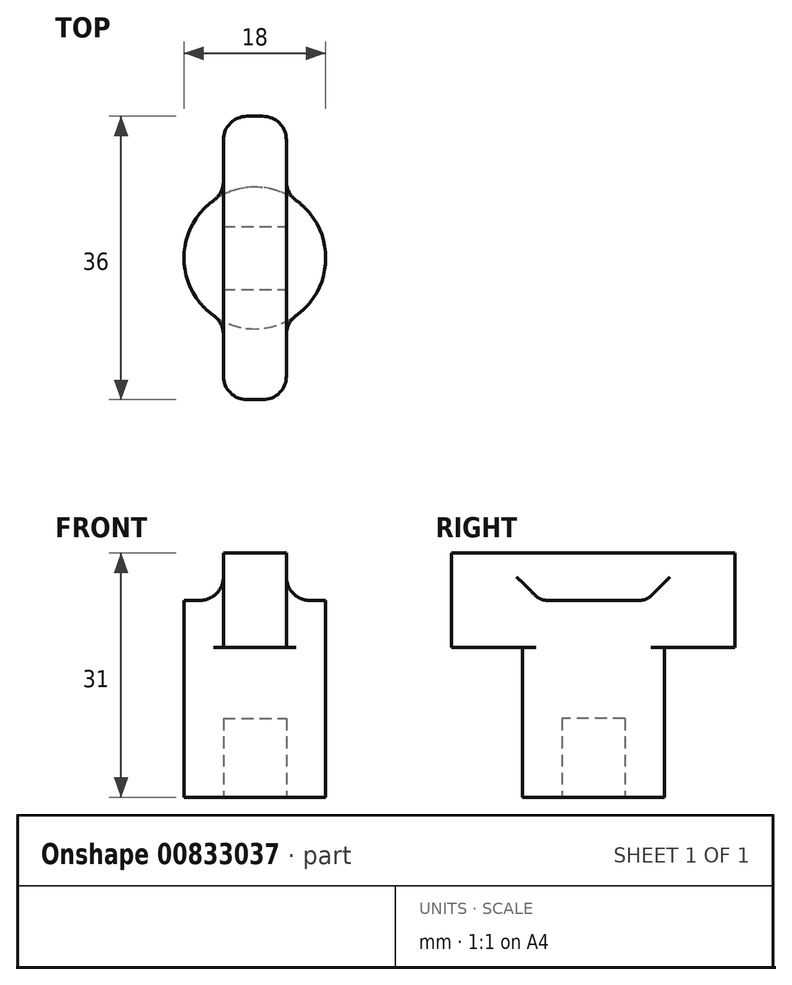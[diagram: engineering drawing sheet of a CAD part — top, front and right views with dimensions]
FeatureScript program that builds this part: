
annotation { "Feature Type Name" : "Feature", "Feature Type Description" : "" }
export const myFeature = defineFeature(function(context is Context, id is Id, definition is map)
    precondition{}
    {
        {
            var Q0;
            Q0=qCreatedBy(makeId("Top.planeOp"),FACE);
            var sketch = newSketch(context, id + "F0", { "sketchPlane" : qUnion([Q0])});
            skCircle(sketch, "E0", {"center": v(0, 0) * mm, "radius": 9 * mm});
            skSolve(sketch);
        }
        {
            var Q0;
            Q0 = qSketchRegion(id + "F0", true);
            extrude(context, id + "F1", {"entities" : qUnion([Q0]), "depth" : 25 * mm, "offsetDistance" : 25 * mm});
        }
        {
            var Q0;
            Q0=makeQuery(id+"F1.opExtrude","CAP_FACE",FACE,{"disambiguationData":[OSD([sQuery(id+"F0.wireOp",EDGE,"E0")])],"isStart":true});
            var sketch = newSketch(context, id + "F2", { "sketchPlane" : qUnion([Q0])});
            skLineSegment(sketch, "E1.bottom", {"start": v(-4, -4) * mm, "end": v(4, -4) * mm});
            skLineSegment(sketch, "E1.top", {"start": v(-4, 4) * mm, "end": v(4, 4) * mm});
            skLineSegment(sketch, "E1.left", {"start": v(-4, -4) * mm, "end": v(-4, 4) * mm});
            skLineSegment(sketch, "E1.right", {"start": v(4, -4) * mm, "end": v(4, 4) * mm});
            skSolve(sketch);
        }
        {
            var Q0;
            Q0 = qSketchRegion(id + "F2", true);
            extrude(context, id + "F3", {"entities" : qUnion([Q0]), "operationType" : NewBodyOperationType.REMOVE, "oppositeDirection" : true, "depth" : 10 * mm, "offsetDistance" : 25 * mm});
        }
        {
            var Q0;
            Q0=makeQuery(id+"F1.opExtrude","CAP_FACE",FACE,{"disambiguationData":[OSD([sQuery(id+"F0.wireOp",EDGE,"E0")])],"isStart":false});
            var sketch = newSketch(context, id + "F4", { "sketchPlane" : qUnion([Q0])});
            skLineSegment(sketch, "E2.bottom", {"start": v(-4, -18) * mm, "end": v(4, -18) * mm});
            skLineSegment(sketch, "E2.top", {"start": v(-4, 18) * mm, "end": v(4, 18) * mm});
            skLineSegment(sketch, "E2.left", {"start": v(-4, -18) * mm, "end": v(-4, 18) * mm});
            skLineSegment(sketch, "E2.right", {"start": v(4, -18) * mm, "end": v(4, 18) * mm});
            skSolve(sketch);
        }
        {
            var Q0;
            Q0 = qSketchRegion(id + "F4", true);
            extrude(context, id + "F5", {"entities" : qUnion([Q0]), "operationType" : NewBodyOperationType.ADD, "endBound" : BoundingType.SYMMETRIC, "depth" : 12 * mm, "offsetDistance" : 25 * mm});
        }
        {
            var Q0;
            Q0=makeQuery(id+"F5.opExtrude","SWEPT_EDGE",EDGE,{"disambiguationData":[OSD([sQuery(id+"F4.wireOp",EDGE,"E2.top"),sQuery(id+"F4.wireOp",EDGE,"E2.left")])]});
            var Q1;
            Q1=makeQuery(id+"F5.opExtrude","SWEPT_EDGE",EDGE,{"disambiguationData":[OSD([sQuery(id+"F4.wireOp",EDGE,"E2.top"),sQuery(id+"F4.wireOp",EDGE,"E2.right")])]});
            var Q2;
            Q2=makeQuery(id+"F5.opExtrude","SWEPT_EDGE",EDGE,{"disambiguationData":[OSD([sQuery(id+"F4.wireOp",EDGE,"E2.bottom"),sQuery(id+"F4.wireOp",EDGE,"E2.left")])]});
            var Q3;
            Q3=makeQuery(id+"F5.opExtrude","SWEPT_EDGE",EDGE,{"disambiguationData":[OSD([sQuery(id+"F4.wireOp",EDGE,"E2.bottom"),sQuery(id+"F4.wireOp",EDGE,"E2.right")])]});
            var Q4;
            Q4=makeQuery(id+"F5.boolean.opBoolean","INTERSECT",EDGE,{"derivedFrom":[makeQuery(id+"F1.opExtrude","CAP_FACE",FACE,{"disambiguationData":[OSD([sQuery(id+"F0.wireOp",EDGE,"E0")])],"isStart":false}),makeQuery(id+"F5.opExtrude","SWEPT_FACE",FACE,{"disambiguationData":[OSD([sQuery(id+"F4.wireOp",EDGE,"E2.left")])]})]});
            var Q5;
            Q5=makeQuery(id+"F5.boolean.opBoolean","INTERSECT",EDGE,{"disambiguationData":[OD(1.0)],"derivedFrom":[makeQuery(id+"F1.opExtrude","SWEPT_FACE",FACE,{"disambiguationData":[OSD([sQuery(id+"F0.wireOp",EDGE,"E0")])]}),makeQuery(id+"F5.opExtrude","SWEPT_FACE",FACE,{"disambiguationData":[OSD([sQuery(id+"F4.wireOp",EDGE,"E2.left")])]})]});
            var Q6;
            Q6=makeQuery(id+"F5.boolean.opBoolean","INTERSECT",EDGE,{"disambiguationData":[OD(0.0)],"derivedFrom":[makeQuery(id+"F1.opExtrude","SWEPT_FACE",FACE,{"disambiguationData":[OSD([sQuery(id+"F0.wireOp",EDGE,"E0")])]}),makeQuery(id+"F5.opExtrude","SWEPT_FACE",FACE,{"disambiguationData":[OSD([sQuery(id+"F4.wireOp",EDGE,"E2.left")])]})]});
            var Q7;
            Q7=makeQuery(id+"F5.boolean.opBoolean","INTERSECT",EDGE,{"disambiguationData":[OD(0.0)],"derivedFrom":[makeQuery(id+"F1.opExtrude","SWEPT_FACE",FACE,{"disambiguationData":[OSD([sQuery(id+"F0.wireOp",EDGE,"E0")])]}),makeQuery(id+"F5.opExtrude","SWEPT_FACE",FACE,{"disambiguationData":[OSD([sQuery(id+"F4.wireOp",EDGE,"E2.right")])]})]});
            var Q8;
            Q8=makeQuery(id+"F5.boolean.opBoolean","INTERSECT",EDGE,{"disambiguationData":[OD(1.0)],"derivedFrom":[makeQuery(id+"F1.opExtrude","SWEPT_FACE",FACE,{"disambiguationData":[OSD([sQuery(id+"F0.wireOp",EDGE,"E0")])]}),makeQuery(id+"F5.opExtrude","SWEPT_FACE",FACE,{"disambiguationData":[OSD([sQuery(id+"F4.wireOp",EDGE,"E2.right")])]})]});
            var Q9;
            Q9=makeQuery(id+"F5.boolean.opBoolean","INTERSECT",EDGE,{"derivedFrom":[makeQuery(id+"F1.opExtrude","CAP_FACE",FACE,{"disambiguationData":[OSD([sQuery(id+"F0.wireOp",EDGE,"E0")])],"isStart":false}),makeQuery(id+"F5.opExtrude","SWEPT_FACE",FACE,{"disambiguationData":[OSD([sQuery(id+"F4.wireOp",EDGE,"E2.right")])]})]});
            fillet(context, id + "F6", {"entities" : qUnion([Q0, Q1, Q2, Q3, Q4, Q5, Q6, Q7, Q8, Q9]), "radius" : 3 * mm, "tangentPropagation" : true, "allowEdgeOverflow" : false});
        }
    });
